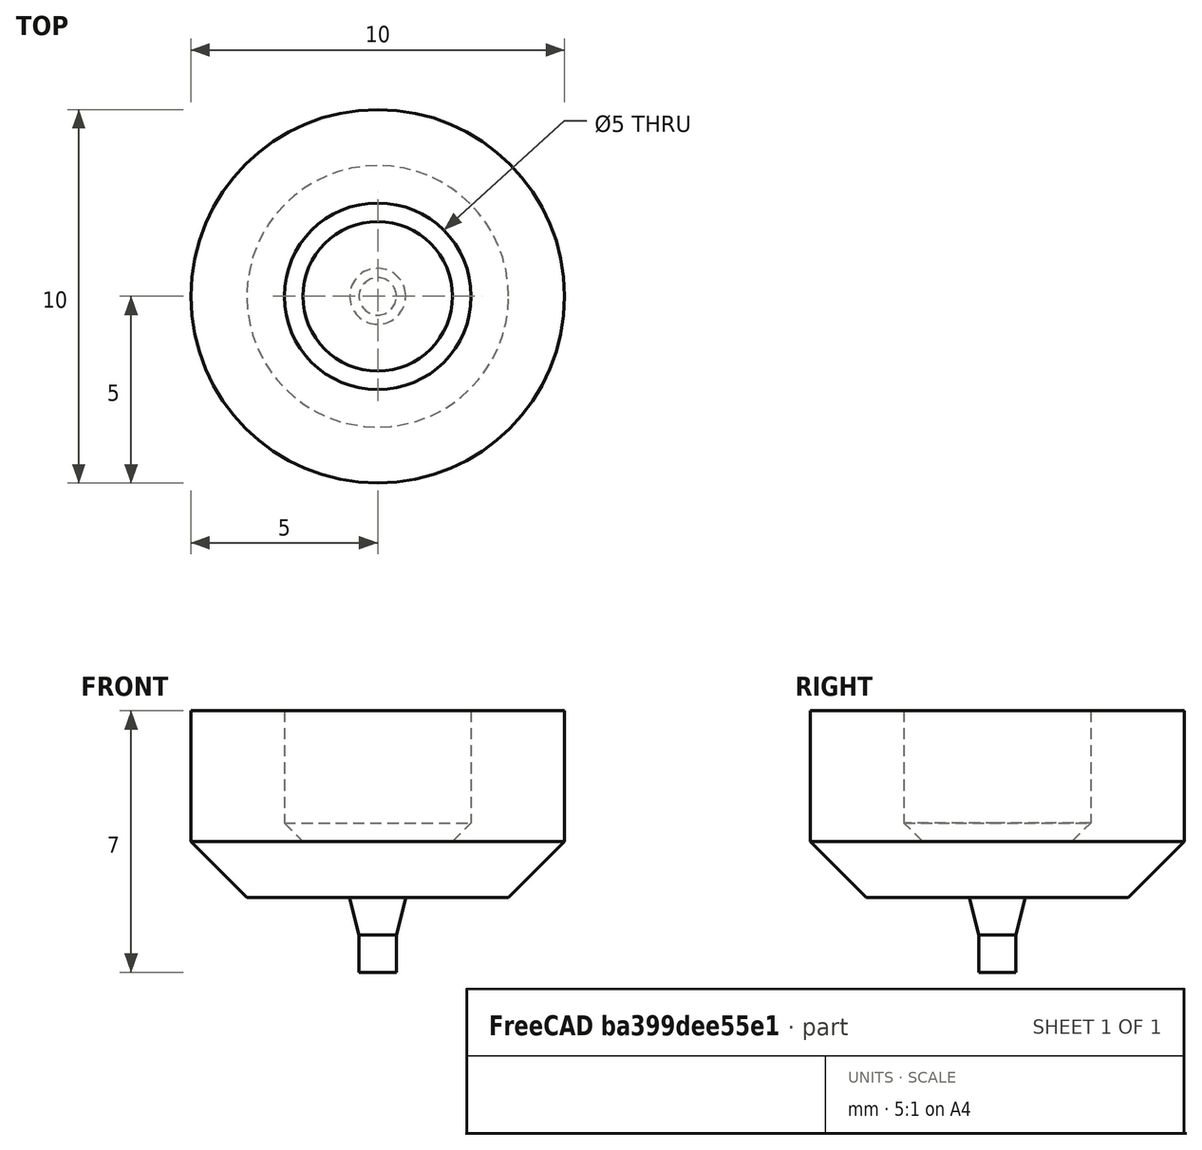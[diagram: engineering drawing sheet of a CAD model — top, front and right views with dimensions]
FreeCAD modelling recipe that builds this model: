
FCSTD DOCUMENT  (FreeCAD 0.20R29603 (Git))
Label: Insert-tool
License: All rights reserved
LicenseURL: http://en.wikipedia.org/wiki/All_rights_reserved
objects: Sketcher::SketchObject×1, PartDesign::Revolution×1, PartDesign::Body×1
note: 4 computed .brp shape members not serialized (recipe doc carries the construction recipe); baked Part::Feature solids carry a one-line shape summary decoded from their .brp

FEATURE [Sketcher::SketchObject] Sketch
  FullyConstrained = true
  MapMode = 5
  Placement = pos=(0,0,0) rot=(1,0,0;1.5708rad)
  Support = -> [XZ_Plane]
  sketch-geometry (15):
    g0: LineSegment StartX=-2.5 StartY=0 StartZ=0 EndX=-2.5 EndY=-3.5 EndZ=0
    g1: LineSegment StartX=-2.5 StartY=0 StartZ=0 EndX=-5 EndY=0 EndZ=0
    g2: LineSegment StartX=-5 StartY=0 StartZ=0 EndX=-5 EndY=-5 EndZ=0
    g3: LineSegment StartX=-2.5 StartY=-3.5 StartZ=0 EndX=0 EndY=-3.5 EndZ=0
    g4: LineSegment StartX=0 StartY=-3.5 StartZ=0 EndX=0 EndY=-7 EndZ=0
    g5: LineSegment StartX=0 StartY=-7 StartZ=0 EndX=-0.5 EndY=-7 EndZ=0
    g6: LineSegment StartX=-0.5 StartY=-7 StartZ=0 EndX=-0.5 EndY=-6 EndZ=0
    g7: LineSegment StartX=-0.5 StartY=-6 StartZ=0 EndX=-0.75 EndY=-5 EndZ=0
    g8: LineSegment StartX=-0.75 StartY=-5 StartZ=0 EndX=-5 EndY=-5 EndZ=0
    g9: LineSegment StartX=-5 StartY=0 StartZ=0 EndX=-5 EndY=-3.5 EndZ=0
    g10: LineSegment StartX=-5 StartY=-3.5 StartZ=0 EndX=-3.5 EndY=-5 EndZ=0
    g11: LineSegment StartX=-3.5 StartY=-5 StartZ=0 EndX=-0.75 EndY=-5 EndZ=0
    g12: LineSegment StartX=-2.5 StartY=0 StartZ=0 EndX=-2.5 EndY=-3 EndZ=0
    g13: LineSegment StartX=-2.5 StartY=-3 StartZ=0 EndX=-2 EndY=-3.5 EndZ=0
    g14: LineSegment StartX=-2 StartY=-3.5 StartZ=0 EndX=0 EndY=-3.5 EndZ=0
  constraints (43):
    c: PointOnObject(g0,g-1)
    c: Vertical(g0)
    c: Coincident(g0,g1)
    c: PointOnObject(g1,g-1)
    c: Coincident(g1,g2)
    c: Vertical(g2)
    c: Coincident(g0,g3)
    c: PointOnObject(g3,g-2)
    c: Horizontal(g3)
    c: Coincident(g3,g4)
    c: Coincident(g4,g5)
    c: Horizontal(g5)
    c: Coincident(g5,g6)
    c: Vertical(g6)
    c: Coincident(g6,g7)
    c: Coincident(g7,g8)
    c: Horizontal(g8)
    c: Coincident(g2,g8)
    c: DistanceX(g0,g-1) = 2.5
    c: DistanceX(g1,g1) = 2.5
    c: DistanceY(g0,g0) = 3.5
    c: PointOnObject(g4,g-2)
    c: DistanceY(g2,g2) = 5
    c: DistanceX(g5,g5) = 0.5
    c: DistanceY(g6,g6) = 1
    c: DistanceX(g7,g4) = 0.75
    c: DistanceY(g7,g7) = 1
    c: Coincident(g1,g9)
    c: Coincident(g9,g10)
    c: Coincident(g10,g11)
    c: Coincident(g11,g7)
    c: Coincident(g1,g12)
    c: Coincident(g12,g13)
    c: Coincident(g13,g14)
    c: Coincident(g14,g4)
    c: PointOnObject(g13,g3)
    c: PointOnObject(g12,g0)
    c: PointOnObject(g10,g8)
    c: PointOnObject(g9,g2)
    c: Angle(g14,g13) = 2.35619
    c: Parallel(g13,g10)
    c: DistanceX(g0,g13) = 0.5
    c: DistanceX(g2,g10) = 1.5
FEATURE [PartDesign::Revolution] Revolution
  Angle = 360
  Axis = (0,2e-16,1)
  Base = (0,0,0)
  Placement = pos=(0,0,0) rot=(1,0,0;1.5708rad)
  Profile = -> Sketch
  ReferenceAxis = -> Sketch [V_Axis]
FEATURE [PartDesign::Body] Body
  Group = -> [Sketch,Revolution]
  Origin = -> Origin
  Tip = -> Revolution
